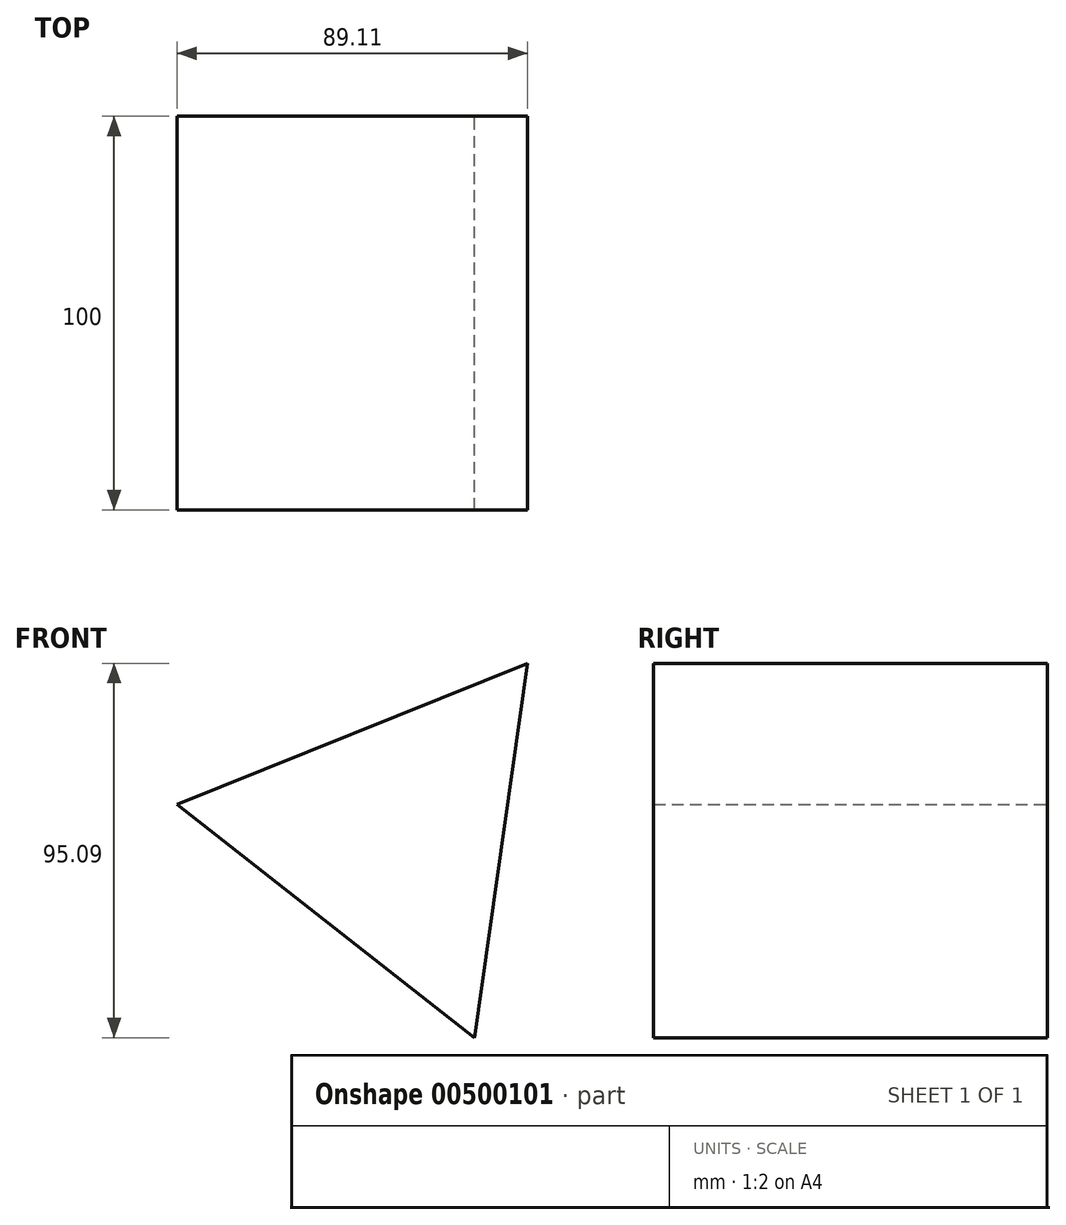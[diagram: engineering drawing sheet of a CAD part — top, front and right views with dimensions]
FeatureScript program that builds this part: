
annotation { "Feature Type Name" : "Feature", "Feature Type Description" : "" }
export const myFeature = defineFeature(function(context is Context, id is Id, definition is map)
    precondition{}
    {
        {
            var Q0;
            Q0=qCreatedBy(makeId("Front.planeOp"),FACE);
            var sketch = newSketch(context, id + "F0", { "sketchPlane" : qUnion([Q0])});
            skCircle(sketch, "E0.cCircle", {"center": v(0, 0) * mm, "radius": 55.45 * mm, "construction": true});
            skLineSegment(sketch, "E0.0", {"start": v(20.7, -51.45) * mm, "end": v(-54.9, 7.8) * mm});
            skLineSegment(sketch, "E0.1", {"start": v(-54.9, 7.8) * mm, "end": v(34.2, 43.64) * mm});
            skLineSegment(sketch, "E0.2", {"start": v(34.2, 43.64) * mm, "end": v(20.7, -51.45) * mm});
            skSolve(sketch);
        }
        {
            var Q0;
            Q0=makeQuery(id+"F0.imprint","IMPRINT",FACE,{"disambiguationData":[TD([[makeQuery(id+"F0.imprint","IMPRINT",EDGE,{"derivedFrom":sQuery(id+"F0.wireOp",EDGE,"E0.0")}),-1.0]])]});
            extrude(context, id + "F1", {"entities" : qUnion([Q0]), "endBound" : BoundingType.SYMMETRIC, "depth" : 100 * mm});
        }
    });
